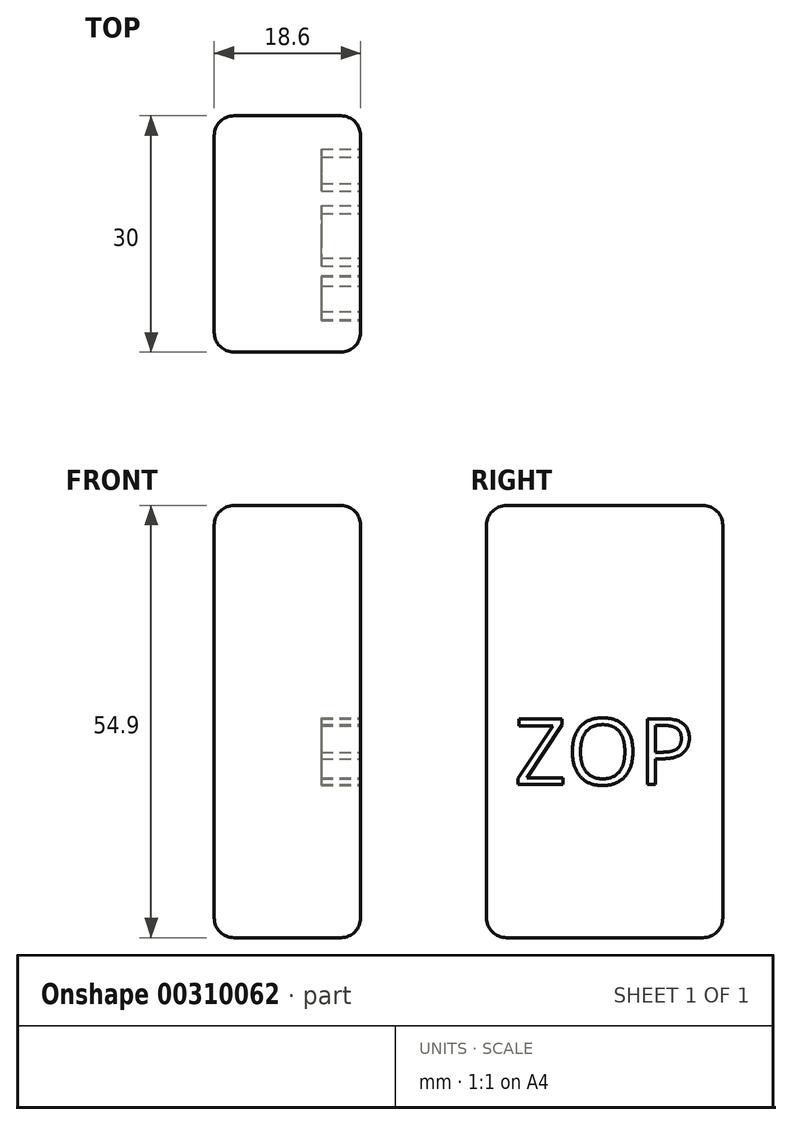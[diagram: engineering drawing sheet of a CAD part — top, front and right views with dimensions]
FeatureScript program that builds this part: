
annotation { "Feature Type Name" : "Feature", "Feature Type Description" : "" }
export const myFeature = defineFeature(function(context is Context, id is Id, definition is map)
    precondition{}
    {
        {
            var Q0;
            Q0=qCreatedBy(makeId("Top.planeOp"),FACE);
            var sketch = newSketch(context, id + "F0", { "sketchPlane" : qUnion([Q0])});
            skLineSegment(sketch, "E0.bottom", {"start": v(9.3, -15) * mm, "end": v(-9.3, -15) * mm});
            skLineSegment(sketch, "E0.top", {"start": v(9.3, 15) * mm, "end": v(-9.3, 15) * mm});
            skLineSegment(sketch, "E0.left", {"start": v(9.3, -15) * mm, "end": v(9.3, 15) * mm});
            skLineSegment(sketch, "E0.right", {"start": v(-9.3, -15) * mm, "end": v(-9.3, 15) * mm});
            skPoint(sketch, "E0.middle", {"position": v(0, 0) * mm});
            skSolve(sketch);
        }
        {
            var Q0;
            Q0=makeQuery(id+"F0.imprint","IMPRINT",FACE,{"disambiguationData":[TD([[makeQuery(id+"F0.imprint","IMPRINT",EDGE,{"derivedFrom":sQuery(id+"F0.wireOp",EDGE,"E0.bottom")}),-1.0]])]});
            extrude(context, id + "F1", {"entities" : qUnion([Q0]), "depth" : 54.9 * mm});
        }
        {
            var Q0;
            Q0=makeQuery(id+"F1.opExtrude","SWEPT_FACE",FACE,{"disambiguationData":[OSD([sQuery(id+"F0.wireOp",EDGE,"E0.top")])]});
            var Q1;
            Q1=makeQuery(id+"F1.opExtrude","CAP_FACE",FACE,{"disambiguationData":[OSD([sQuery(id+"F0.wireOp",EDGE,"E0.bottom"),sQuery(id+"F0.wireOp",EDGE,"E0.top"),sQuery(id+"F0.wireOp",EDGE,"E0.left"),sQuery(id+"F0.wireOp",EDGE,"E0.right")])],"isStart":false});
            var Q2;
            Q2=makeQuery(id+"F1.opExtrude","SWEPT_FACE",FACE,{"disambiguationData":[OSD([sQuery(id+"F0.wireOp",EDGE,"E0.bottom")])]});
            var Q3;
            Q3=makeQuery(id+"F1.opExtrude","CAP_FACE",FACE,{"disambiguationData":[OSD([sQuery(id+"F0.wireOp",EDGE,"E0.bottom"),sQuery(id+"F0.wireOp",EDGE,"E0.top"),sQuery(id+"F0.wireOp",EDGE,"E0.left"),sQuery(id+"F0.wireOp",EDGE,"E0.right")])],"isStart":true});
            fillet(context, id + "F2", {"entities" : qUnion([Q0, Q1, Q2, Q3]), "radius" : 2.5 * mm, "tangentPropagation" : true, "allowEdgeOverflow" : false});
        }
        {
            var Q0;
            Q0=makeQuery(id+"F1.opExtrude","SWEPT_FACE",FACE,{"disambiguationData":[OSD([sQuery(id+"F0.wireOp",EDGE,"E0.left")])]});
            var sketch = newSketch(context, id + "F3", { "sketchPlane" : qUnion([Q0])});
            skText(sketch, "E1", { "text": "ZOP", "fontName": "OpenSans-Regular.ttf"});
            const initialGuessF3  = {"E1": [-0.0115, 0.01944, 1, 0, 0.00843]};
            skSetInitialGuess(sketch, initialGuessF3);
            skSolve(sketch);
        }
        {
            var Q0;
            Q0=makeQuery(id+"F3.imprint","IMPRINT",FACE,{"disambiguationData":[TD([[makeQuery(id+"F3.imprint","IMPRINT",EDGE,{"derivedFrom":sQuery(id+"F3.wireOp",EDGE,"E1.sketch_text.stroke-0")}),-1.0]])]});
            var Q1;
            Q1=makeQuery(id+"F3.imprint","IMPRINT",FACE,{"disambiguationData":[TD([[makeQuery(id+"F3.imprint","IMPRINT",EDGE,{"derivedFrom":sQuery(id+"F3.wireOp",EDGE,"E1.sketch_text.stroke-10")}),-1.0]])]});
            var Q2;
            Q2=makeQuery(id+"F3.imprint","IMPRINT",FACE,{"disambiguationData":[TD([[makeQuery(id+"F3.imprint","IMPRINT",EDGE,{"derivedFrom":sQuery(id+"F3.wireOp",EDGE,"E1.sketch_text.stroke-26")}),-1.0]])]});
            extrude(context, id + "F4", {"entities" : qUnion([Q0, Q1, Q2]), "operationType" : NewBodyOperationType.REMOVE, "oppositeDirection" : true, "depth" : 5 * mm});
        }
    });
